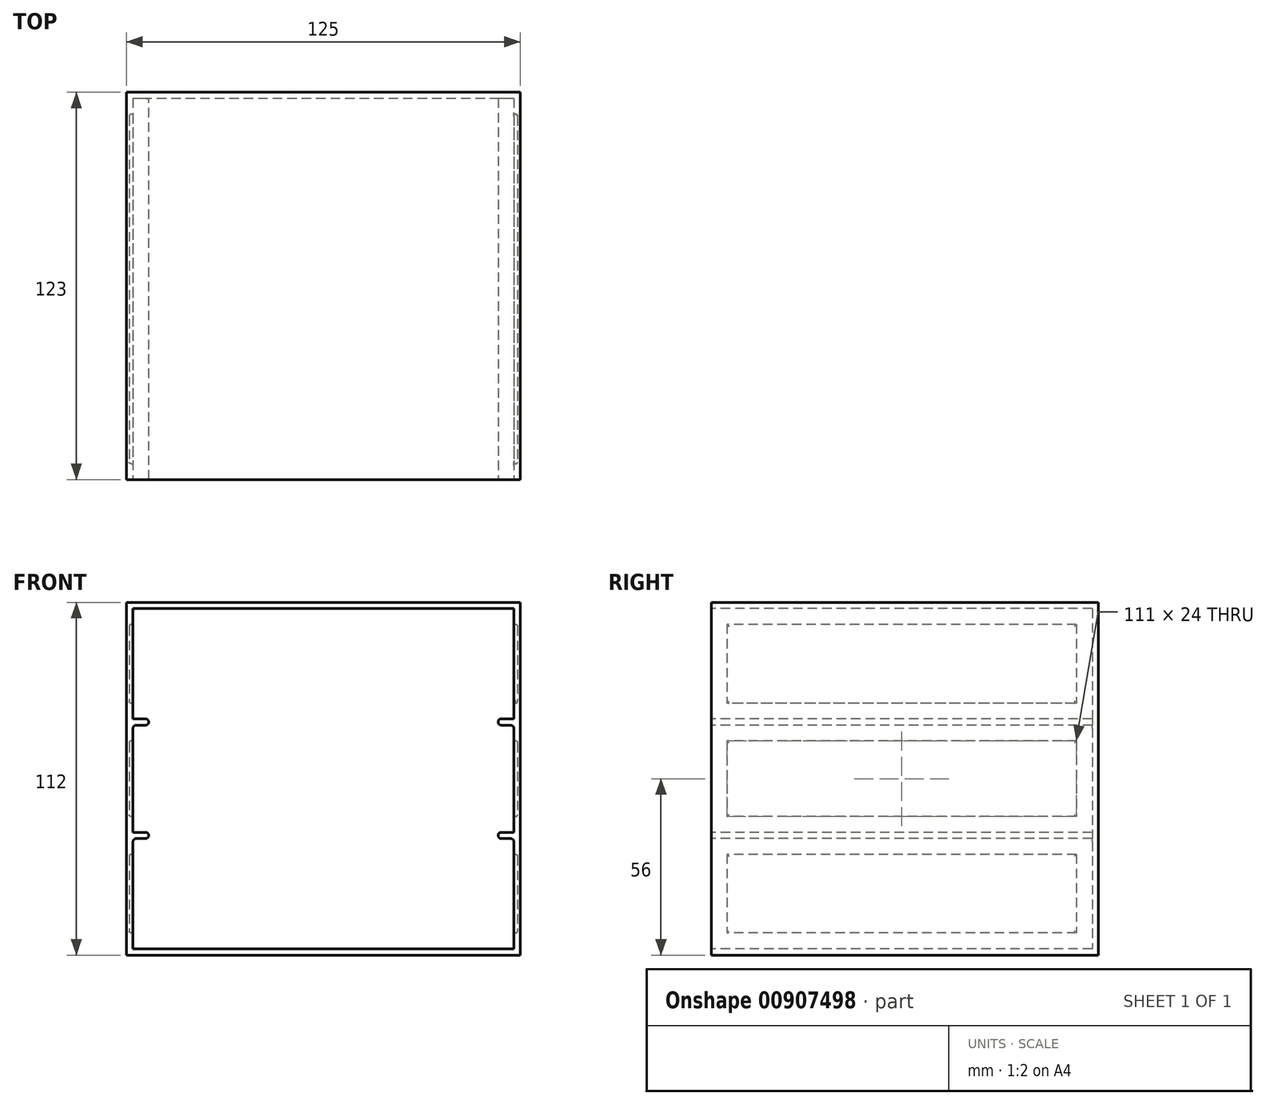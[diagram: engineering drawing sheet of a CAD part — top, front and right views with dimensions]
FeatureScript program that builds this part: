
annotation { "Feature Type Name" : "Feature", "Feature Type Description" : "" }
export const myFeature = defineFeature(function(context is Context, id is Id, definition is map)
    precondition{}
    {
        {
            var Q0;
            Q0=qCreatedBy(makeId("Top.planeOp"),FACE);
            var sketch = newSketch(context, id + "F0", { "sketchPlane" : qUnion([Q0])});
            skLineSegment(sketch, "E0.bottom", {"start": v(62.5, 61) * mm, "end": v(-62.5, 61) * mm});
            skLineSegment(sketch, "E0.top", {"start": v(62.5, -61) * mm, "end": v(-62.5, -61) * mm});
            skLineSegment(sketch, "E0.left", {"start": v(62.5, 61) * mm, "end": v(62.5, -61) * mm});
            skLineSegment(sketch, "E0.right", {"start": v(-62.5, 61) * mm, "end": v(-62.5, -61) * mm});
            skPoint(sketch, "E0.middle", {"position": v(0, 0) * mm});
            skSolve(sketch);
        }
        {
            var Q0;
            Q0=makeQuery(id+"F0.imprint","IMPRINT",FACE,{"disambiguationData":[TD([[makeQuery(id+"F0.imprint","IMPRINT",EDGE,{"derivedFrom":sQuery(id+"F0.wireOp",EDGE,"E0.bottom")}),1.0]])]});
            extrude(context, id + "F1", {"entities" : qUnion([Q0]), "depth" : 2 * mm, "offsetDistance" : 25 * mm});
        }
        {
            var Q0;
            Q0=makeQuery(id+"F1.opExtrude","CAP_FACE",FACE,{"disambiguationData":[OSD([sQuery(id+"F0.wireOp",EDGE,"E0.bottom"),sQuery(id+"F0.wireOp",EDGE,"E0.top"),sQuery(id+"F0.wireOp",EDGE,"E0.left"),sQuery(id+"F0.wireOp",EDGE,"E0.right")])],"isStart":false});
            var sketch = newSketch(context, id + "F2", { "sketchPlane" : qUnion([Q0])});
            skLineSegment(sketch, "E1.0", {"start": v(-60.5, 61) * mm, "end": v(-60.5, -61) * mm});
            skLineSegment(sketch, "E2.0", {"start": v(62.5, 59) * mm, "end": v(-62.5, 59) * mm});
            skLineSegment(sketch, "E3.0", {"start": v(60.5, 61) * mm, "end": v(60.5, -61) * mm});
            skSolve(sketch);
        }
        {
            var Q0;
            Q0=qSketchRegion(id+"F2",true);
            var Q1;
            {var subQ0=sQuery(id+"F2.wireOp",EDGE,"E1.0");var subQ1=makeQuery(id+"F1.opExtrude","CAP_EDGE",EDGE,{"disambiguationData":[OSD([sQuery(id+"F0.wireOp",EDGE,"E0.bottom")])],"isStart":false});var subQ2=makeQuery(id+"F2.imprint","INTERSECT",VERTEX,{"derivedFrom":[subQ1,subQ0]});Q1=makeQuery(id+"F2.imprint","IMPRINT",FACE,{"disambiguationData":[TD([[makeQuery(id+"F2.imprint","IMPRINT",EDGE,{"disambiguationData":[TD([[subQ2,-1.0]])],"derivedFrom":subQ0}),1.0]])]});}
            var Q2;
            {var subQ0=sQuery(id+"F2.wireOp",EDGE,"E1.0");var subQ1=makeQuery(id+"F1.opExtrude","CAP_EDGE",EDGE,{"disambiguationData":[OSD([sQuery(id+"F0.wireOp",EDGE,"E0.bottom")])],"isStart":false});var subQ2=makeQuery(id+"F2.imprint","INTERSECT",VERTEX,{"derivedFrom":[subQ1,subQ0]});Q2=makeQuery(id+"F2.imprint","IMPRINT",FACE,{"disambiguationData":[TD([[makeQuery(id+"F2.imprint","IMPRINT",EDGE,{"disambiguationData":[TD([[subQ2,-1.0]])],"derivedFrom":subQ0}),-1.0]])]});}
            var Q3;
            {var subQ0=sQuery(id+"F2.wireOp",EDGE,"E1.0");var subQ1=makeQuery(id+"F1.opExtrude","CAP_EDGE",EDGE,{"disambiguationData":[OSD([sQuery(id+"F0.wireOp",EDGE,"E0.top")])],"isStart":false});var subQ2=makeQuery(id+"F2.imprint","INTERSECT",VERTEX,{"derivedFrom":[subQ1,subQ0]});Q3=makeQuery(id+"F2.imprint","IMPRINT",FACE,{"disambiguationData":[TD([[makeQuery(id+"F2.imprint","IMPRINT",EDGE,{"disambiguationData":[TD([[subQ2,1.0]])],"derivedFrom":subQ0}),-1.0]])]});}
            var Q4;
            {var subQ0=sQuery(id+"F2.wireOp",EDGE,"E2.0");var subQ1=makeQuery(id+"F1.opExtrude","CAP_EDGE",EDGE,{"disambiguationData":[OSD([sQuery(id+"F0.wireOp",EDGE,"E0.left")])],"isStart":false});var subQ2=makeQuery(id+"F2.imprint","INTERSECT",VERTEX,{"derivedFrom":[subQ1,subQ0]});Q4=makeQuery(id+"F2.imprint","IMPRINT",FACE,{"disambiguationData":[TD([[makeQuery(id+"F2.imprint","IMPRINT",EDGE,{"disambiguationData":[TD([[subQ2,-1.0]])],"derivedFrom":subQ0}),1.0]])]});}
            var Q5;
            {var subQ0=sQuery(id+"F2.wireOp",EDGE,"E2.0");var subQ1=makeQuery(id+"F1.opExtrude","CAP_EDGE",EDGE,{"disambiguationData":[OSD([sQuery(id+"F0.wireOp",EDGE,"E0.left")])],"isStart":false});var subQ2=makeQuery(id+"F2.imprint","INTERSECT",VERTEX,{"derivedFrom":[subQ1,subQ0]});Q5=makeQuery(id+"F2.imprint","IMPRINT",FACE,{"disambiguationData":[TD([[makeQuery(id+"F2.imprint","IMPRINT",EDGE,{"disambiguationData":[TD([[subQ2,-1.0]])],"derivedFrom":subQ0}),-1.0]])]});}
            extrude(context, id + "F3", {"entities" : qUnion([Q0, Q1, Q2, Q3, Q4, Q5]), "operationType" : NewBodyOperationType.ADD, "depth" : 108 * mm, "offsetDistance" : 25 * mm});
        }
        {
            var Q0;
            Q0=makeQuery(id+"F3.opExtrude","CAP_FACE",FACE,{"disambiguationData":[OSD([sQuery(id+"F0.wireOp",EDGE,"E0.bottom"),sQuery(id+"F0.wireOp",EDGE,"E0.top"),sQuery(id+"F0.wireOp",EDGE,"E0.left"),sQuery(id+"F0.wireOp",EDGE,"E0.right"),sQuery(id+"F2.wireOp",EDGE,"E1.0"),sQuery(id+"F2.wireOp",EDGE,"E2.0"),sQuery(id+"F2.wireOp",EDGE,"E3.0")])],"isStart":false});
            var sketch = newSketch(context, id + "F4", { "sketchPlane" : qUnion([Q0])});
            skLineSegment(sketch, "E4.bottom", {"start": v(-62.5, 61) * mm, "end": v(62.5, 61) * mm});
            skLineSegment(sketch, "E4.top", {"start": v(-62.5, -61) * mm, "end": v(62.5, -61) * mm});
            skLineSegment(sketch, "E4.left", {"start": v(-62.5, 61) * mm, "end": v(-62.5, -61) * mm});
            skLineSegment(sketch, "E4.right", {"start": v(62.5, 61) * mm, "end": v(62.5, -61) * mm});
            skSolve(sketch);
        }
        {
            var Q0;
            Q0=qSketchRegion(id+"F4",true);
            extrude(context, id + "F5", {"entities" : qUnion([Q0]), "operationType" : NewBodyOperationType.ADD, "depth" : 2 * mm, "offsetDistance" : 25 * mm});
        }
        {
            var Q0;
            {var subQ0=sQuery(id+"F0.wireOp",EDGE,"E0.top");var subQ1=makeQuery(id+"F1.opExtrude","CAP_EDGE",EDGE,{"disambiguationData":[OSD([subQ0])],"isStart":false});Q0=makeQuery(id+"F5.boolean.opBoolean","MERGE",FACE,{"derivedFrom":[makeQuery(id+"F3.boolean.opBoolean","MERGE",FACE,{"derivedFrom":[makeQuery(id+"F1.opExtrude","SWEPT_FACE",FACE,{"disambiguationData":[OSD([subQ0])]}),makeQuery(id+"F3.opExtrude","SWEPT_FACE",FACE,{"disambiguationData":[OSD([subQ0]),TDD([makeQuery(id+"F2.imprint","IMPRINT",EDGE,{"disambiguationData":[TD([[makeQuery(id+"F2.imprint","INTERSECT",VERTEX,{"derivedFrom":[subQ1,makeQuery(id+"F1.opExtrude","CAP_EDGE",EDGE,{"disambiguationData":[OSD([sQuery(id+"F0.wireOp",EDGE,"E0.left")])],"isStart":false})]}),-1.0]])],"derivedFrom":subQ1})])]}),makeQuery(id+"F3.opExtrude","SWEPT_FACE",FACE,{"disambiguationData":[OSD([subQ0]),TDD([makeQuery(id+"F2.imprint","IMPRINT",EDGE,{"disambiguationData":[TD([[makeQuery(id+"F2.imprint","INTERSECT",VERTEX,{"derivedFrom":[subQ1,makeQuery(id+"F1.opExtrude","CAP_EDGE",EDGE,{"disambiguationData":[OSD([sQuery(id+"F0.wireOp",EDGE,"E0.right")])],"isStart":false})]}),1.0]])],"derivedFrom":subQ1})])]})]}),makeQuery(id+"F5.opExtrude","SWEPT_FACE",FACE,{"disambiguationData":[OSD([sQuery(id+"F4.wireOp",EDGE,"E4.top")])]})]});}
            var sketch = newSketch(context, id + "F6", { "sketchPlane" : qUnion([Q0])});
            skLineSegment(sketch, "E5.0", {"start": v(60.5, 38) * mm, "end": v(-60.5, 38) * mm});
            skLineSegment(sketch, "E6.0", {"start": v(60.5, 74) * mm, "end": v(-60.5, 74) * mm});
            skLineSegment(sketch, "E7.0", {"start": v(60.5, 39) * mm, "end": v(-60.5, 39) * mm});
            skLineSegment(sketch, "E8.0", {"start": v(60.5, 37) * mm, "end": v(-60.5, 37) * mm});
            skLineSegment(sketch, "E9.0", {"start": v(60.5, 75) * mm, "end": v(-60.5, 75) * mm});
            skLineSegment(sketch, "E10.0", {"start": v(60.5, 73) * mm, "end": v(-60.5, 73) * mm});
            skLineSegment(sketch, "E11.0", {"start": v(-55.5, 110) * mm, "end": v(-55.5, 2) * mm});
            skLineSegment(sketch, "E12.0", {"start": v(55.5, 110) * mm, "end": v(55.5, 2) * mm});
            skSolve(sketch);
        }
        {
            var Q0;
            {var subQ0=sQuery(id+"F6.wireOp",EDGE,"E6.0");var subQ3=sQuery(id+"F6.wireOp",EDGE,"E11.0");var subQ4=makeQuery(id+"F6.imprint","INTERSECT",VERTEX,{"derivedFrom":[subQ0,subQ3]});Q0=makeQuery(id+"F6.imprint","IMPRINT",FACE,{"disambiguationData":[TD([[makeQuery(id+"F6.imprint","IMPRINT",EDGE,{"disambiguationData":[TD([[subQ4,1.0]])],"derivedFrom":subQ3}),-1.0]])]});}
            var Q1;
            {var subQ0=sQuery(id+"F6.wireOp",EDGE,"E6.0");var subQ3=sQuery(id+"F6.wireOp",EDGE,"E11.0");var subQ4=makeQuery(id+"F6.imprint","INTERSECT",VERTEX,{"derivedFrom":[subQ0,subQ3]});Q1=makeQuery(id+"F6.imprint","IMPRINT",FACE,{"disambiguationData":[TD([[makeQuery(id+"F6.imprint","IMPRINT",EDGE,{"disambiguationData":[TD([[subQ4,-1.0]])],"derivedFrom":subQ3}),-1.0]])]});}
            var Q2;
            {var subQ0=sQuery(id+"F6.wireOp",EDGE,"E5.0");var subQ3=sQuery(id+"F6.wireOp",EDGE,"E11.0");var subQ4=makeQuery(id+"F6.imprint","INTERSECT",VERTEX,{"derivedFrom":[subQ0,subQ3]});Q2=makeQuery(id+"F6.imprint","IMPRINT",FACE,{"disambiguationData":[TD([[makeQuery(id+"F6.imprint","IMPRINT",EDGE,{"disambiguationData":[TD([[subQ4,1.0]])],"derivedFrom":subQ3}),-1.0]])]});}
            var Q3;
            {var subQ0=sQuery(id+"F6.wireOp",EDGE,"E5.0");var subQ3=sQuery(id+"F6.wireOp",EDGE,"E11.0");var subQ4=makeQuery(id+"F6.imprint","INTERSECT",VERTEX,{"derivedFrom":[subQ0,subQ3]});Q3=makeQuery(id+"F6.imprint","IMPRINT",FACE,{"disambiguationData":[TD([[makeQuery(id+"F6.imprint","IMPRINT",EDGE,{"disambiguationData":[TD([[subQ4,-1.0]])],"derivedFrom":subQ3}),-1.0]])]});}
            var Q4;
            {var subQ0=sQuery(id+"F6.wireOp",EDGE,"E6.0");var subQ3=sQuery(id+"F6.wireOp",EDGE,"E12.0");var subQ4=makeQuery(id+"F6.imprint","INTERSECT",VERTEX,{"derivedFrom":[subQ0,subQ3]});Q4=makeQuery(id+"F6.imprint","IMPRINT",FACE,{"disambiguationData":[TD([[makeQuery(id+"F6.imprint","IMPRINT",EDGE,{"disambiguationData":[TD([[subQ4,1.0]])],"derivedFrom":subQ3}),1.0]])]});}
            var Q5;
            {var subQ0=sQuery(id+"F6.wireOp",EDGE,"E6.0");var subQ3=sQuery(id+"F6.wireOp",EDGE,"E12.0");var subQ4=makeQuery(id+"F6.imprint","INTERSECT",VERTEX,{"derivedFrom":[subQ0,subQ3]});Q5=makeQuery(id+"F6.imprint","IMPRINT",FACE,{"disambiguationData":[TD([[makeQuery(id+"F6.imprint","IMPRINT",EDGE,{"disambiguationData":[TD([[subQ4,-1.0]])],"derivedFrom":subQ3}),1.0]])]});}
            var Q6;
            {var subQ0=sQuery(id+"F6.wireOp",EDGE,"E5.0");var subQ3=sQuery(id+"F6.wireOp",EDGE,"E12.0");var subQ4=makeQuery(id+"F6.imprint","INTERSECT",VERTEX,{"derivedFrom":[subQ0,subQ3]});Q6=makeQuery(id+"F6.imprint","IMPRINT",FACE,{"disambiguationData":[TD([[makeQuery(id+"F6.imprint","IMPRINT",EDGE,{"disambiguationData":[TD([[subQ4,1.0]])],"derivedFrom":subQ3}),1.0]])]});}
            var Q7;
            {var subQ0=sQuery(id+"F6.wireOp",EDGE,"E5.0");var subQ3=sQuery(id+"F6.wireOp",EDGE,"E12.0");var subQ4=makeQuery(id+"F6.imprint","INTERSECT",VERTEX,{"derivedFrom":[subQ0,subQ3]});Q7=makeQuery(id+"F6.imprint","IMPRINT",FACE,{"disambiguationData":[TD([[makeQuery(id+"F6.imprint","IMPRINT",EDGE,{"disambiguationData":[TD([[subQ4,-1.0]])],"derivedFrom":subQ3}),1.0]])]});}
            extrude(context, id + "F7", {"entities" : qUnion([Q0, Q1, Q2, Q3, Q4, Q5, Q6, Q7]), "operationType" : NewBodyOperationType.ADD, "oppositeDirection" : true, "depth" : 120 * mm, "offsetDistance" : 25 * mm});
        }
        {
            var Q0;
            {var subQ0=sQuery(id+"F6.wireOp",EDGE,"E11.0");var subQ1=sQuery(id+"F6.wireOp",EDGE,"E10.0");var subQ2=sQuery(id+"F6.wireOp",EDGE,"E9.0");var subQ3=sQuery(id+"F2.wireOp",EDGE,"E1.0");var subQ4=sQuery(id+"F0.wireOp",EDGE,"E0.top");var subQ5=sQuery(id+"F6.wireOp",EDGE,"E12.0");var subQ6=sQuery(id+"F2.wireOp",EDGE,"E3.0");var subQ7=sQuery(id+"F6.wireOp",EDGE,"E8.0");var subQ8=sQuery(id+"F6.wireOp",EDGE,"E7.0");var subQ9=makeQuery(id+"F1.opExtrude","CAP_EDGE",EDGE,{"disambiguationData":[OSD([subQ4])],"isStart":false});Q0=makeQuery(id+"F7.boolean.opBoolean","MERGE",FACE,{"derivedFrom":[makeQuery(id+"F5.boolean.opBoolean","MERGE",FACE,{"derivedFrom":[makeQuery(id+"F3.boolean.opBoolean","MERGE",FACE,{"derivedFrom":[makeQuery(id+"F1.opExtrude","SWEPT_FACE",FACE,{"disambiguationData":[OSD([subQ4])]}),makeQuery(id+"F3.opExtrude","SWEPT_FACE",FACE,{"disambiguationData":[OSD([subQ4]),TDD([makeQuery(id+"F2.imprint","IMPRINT",EDGE,{"disambiguationData":[TD([[makeQuery(id+"F2.imprint","INTERSECT",VERTEX,{"derivedFrom":[subQ9,makeQuery(id+"F1.opExtrude","CAP_EDGE",EDGE,{"disambiguationData":[OSD([sQuery(id+"F0.wireOp",EDGE,"E0.left")])],"isStart":false})]}),-1.0]])],"derivedFrom":subQ9})])]}),makeQuery(id+"F3.opExtrude","SWEPT_FACE",FACE,{"disambiguationData":[OSD([subQ4]),TDD([makeQuery(id+"F2.imprint","IMPRINT",EDGE,{"disambiguationData":[TD([[makeQuery(id+"F2.imprint","INTERSECT",VERTEX,{"derivedFrom":[subQ9,makeQuery(id+"F1.opExtrude","CAP_EDGE",EDGE,{"disambiguationData":[OSD([sQuery(id+"F0.wireOp",EDGE,"E0.right")])],"isStart":false})]}),1.0]])],"derivedFrom":subQ9})])]})]}),makeQuery(id+"F5.opExtrude","SWEPT_FACE",FACE,{"disambiguationData":[OSD([sQuery(id+"F4.wireOp",EDGE,"E4.top")])]})]}),makeQuery(id+"F7.opExtrude","CAP_FACE",FACE,{"disambiguationData":[OSD([subQ4,subQ6,subQ8,subQ7,subQ5])],"isStart":true}),makeQuery(id+"F7.opExtrude","CAP_FACE",FACE,{"disambiguationData":[OSD([subQ4,subQ3,subQ8,subQ7,subQ0])],"isStart":true}),makeQuery(id+"F7.opExtrude","CAP_FACE",FACE,{"disambiguationData":[OSD([subQ4,subQ6,subQ2,subQ1,subQ5])],"isStart":true}),makeQuery(id+"F7.opExtrude","CAP_FACE",FACE,{"disambiguationData":[OSD([subQ4,subQ3,subQ2,subQ1,subQ0])],"isStart":true})]});}
            extrude(context, id + "F8", {"entities" : qUnion([Q0]), "operationType" : NewBodyOperationType.ADD, "depth" : 1 * mm, "offsetDistance" : 25 * mm});
        }
        {
            var Q0;
            {var subQ0=sQuery(id+"F6.wireOp",EDGE,"E9.0");var subQ1=sQuery(id+"F2.wireOp",EDGE,"E1.0");var subQ2=sQuery(id+"F0.wireOp",EDGE,"E0.top");var subQ3=makeQuery(id+"F3.opExtrude","SWEPT_EDGE",EDGE,{"disambiguationData":[OSD([subQ2,subQ1])]});var subQ4=sQuery(id+"F6.wireOp",EDGE,"E11.0");var subQ5=makeQuery(id+"F7.opExtrude","SWEPT_FACE",FACE,{"disambiguationData":[OSD([subQ0]),TDD([makeQuery(id+"F6.imprint","IMPRINT",EDGE,{"disambiguationData":[TD([[makeQuery(id+"F6.imprint","INTERSECT",VERTEX,{"derivedFrom":[subQ0,subQ4]}),-1.0]])],"derivedFrom":subQ0})])]});var subQ20=makeQuery(id+"F3.opExtrude","SWEPT_FACE",FACE,{"disambiguationData":[OSD([subQ1])]});Q0=makeQuery(id+"F8.boolean.opBoolean","MERGE",FACE,{"derivedFrom":[makeQuery(id+"F7.boolean.opBoolean","SPLIT",FACE,{"disambiguationData":[TD([subQ5])],"derivedFrom":subQ20}),makeQuery(id+"F8.opExtrude","SWEPT_FACE",FACE,{"disambiguationData":[OSD([subQ2,subQ1]),TDD([makeQuery(id+"F7.boolean.opBoolean","SPLIT",EDGE,{"disambiguationData":[TD([subQ5])],"derivedFrom":subQ3})])]})]});}
            var sketch = newSketch(context, id + "F9", { "sketchPlane" : qUnion([Q0])});
            skLineSegment(sketch, "E13.0", {"start": v(54, 105) * mm, "end": v(-57, 105) * mm});
            skLineSegment(sketch, "E13.1", {"start": v(54, 105) * mm, "end": v(54, 80) * mm});
            skLineSegment(sketch, "E13.2", {"start": v(54, 80) * mm, "end": v(-57, 80) * mm});
            skLineSegment(sketch, "E13.3", {"start": v(-57, 105) * mm, "end": v(-57, 80) * mm});
            skLineSegment(sketch, "E14.0", {"start": v(54, 68) * mm, "end": v(-57, 68) * mm});
            skLineSegment(sketch, "E14.1", {"start": v(54, 68) * mm, "end": v(54, 44) * mm});
            skLineSegment(sketch, "E14.2", {"start": v(54, 44) * mm, "end": v(-57, 44) * mm});
            skLineSegment(sketch, "E14.3", {"start": v(-57, 68) * mm, "end": v(-57, 44) * mm});
            skLineSegment(sketch, "E15.0", {"start": v(54, 32) * mm, "end": v(-57, 32) * mm});
            skLineSegment(sketch, "E15.1", {"start": v(54, 32) * mm, "end": v(54, 7) * mm});
            skLineSegment(sketch, "E15.2", {"start": v(54, 7) * mm, "end": v(-57, 7) * mm});
            skLineSegment(sketch, "E15.3", {"start": v(-57, 32) * mm, "end": v(-57, 7) * mm});
            skSolve(sketch);
        }
        {
            var Q0;
            {var subQ4=sQuery(id+"F0.wireOp",EDGE,"E0.top");var subQ8=sQuery(id+"F6.wireOp",EDGE,"E12.0");var subQ9=sQuery(id+"F2.wireOp",EDGE,"E3.0");var subQ11=makeQuery(id+"F3.opExtrude","SWEPT_FACE",FACE,{"disambiguationData":[OSD([subQ9])]});var subQ13=sQuery(id+"F6.wireOp",EDGE,"E9.0");var subQ20=makeQuery(id+"F3.opExtrude","SWEPT_EDGE",EDGE,{"disambiguationData":[OSD([subQ4,subQ9])]});var subQ21=makeQuery(id+"F7.opExtrude","SWEPT_FACE",FACE,{"disambiguationData":[OSD([subQ13]),TDD([makeQuery(id+"F6.imprint","IMPRINT",EDGE,{"disambiguationData":[TD([[makeQuery(id+"F6.imprint","INTERSECT",VERTEX,{"derivedFrom":[subQ13,subQ8]}),1.0]])],"derivedFrom":subQ13})])]});Q0=makeQuery(id+"F8.boolean.opBoolean","MERGE",FACE,{"derivedFrom":[makeQuery(id+"F7.boolean.opBoolean","SPLIT",FACE,{"disambiguationData":[TD([subQ21])],"derivedFrom":subQ11}),makeQuery(id+"F8.opExtrude","SWEPT_FACE",FACE,{"disambiguationData":[OSD([subQ4,subQ9]),TDD([makeQuery(id+"F7.boolean.opBoolean","SPLIT",EDGE,{"disambiguationData":[TD([subQ21])],"derivedFrom":subQ20})])]})]});}
            var sketch = newSketch(context, id + "F10", { "sketchPlane" : qUnion([Q0])});
            skLineSegment(sketch, "E16.0", {"start": v(-54, 105) * mm, "end": v(57, 105) * mm});
            skLineSegment(sketch, "E16.1", {"start": v(-54, 105) * mm, "end": v(-54, 80) * mm});
            skLineSegment(sketch, "E16.2", {"start": v(-54, 80) * mm, "end": v(57, 80) * mm});
            skLineSegment(sketch, "E16.3", {"start": v(57, 105) * mm, "end": v(57, 80) * mm});
            skLineSegment(sketch, "E17.0", {"start": v(-54, 68) * mm, "end": v(57, 68) * mm});
            skLineSegment(sketch, "E17.1", {"start": v(-54, 68) * mm, "end": v(-54, 44) * mm});
            skLineSegment(sketch, "E17.2", {"start": v(-54, 44) * mm, "end": v(57, 44) * mm});
            skLineSegment(sketch, "E17.3", {"start": v(57, 68) * mm, "end": v(57, 44) * mm});
            skLineSegment(sketch, "E18.0", {"start": v(57, 32) * mm, "end": v(57, 7) * mm});
            skLineSegment(sketch, "E18.1", {"start": v(-54, 32) * mm, "end": v(57, 32) * mm});
            skLineSegment(sketch, "E18.2", {"start": v(-54, 32) * mm, "end": v(-54, 7) * mm});
            skLineSegment(sketch, "E18.3", {"start": v(-54, 7) * mm, "end": v(57, 7) * mm});
            skSolve(sketch);
        }
        {
            var Q0;
            Q0 = qSketchRegion(id + "F9", true);
            extrude(context, id + "F11", {"entities" : qUnion([Q0]), "operationType" : NewBodyOperationType.REMOVE, "oppositeDirection" : true, "depth" : 1.2 * mm, "offsetDistance" : 25 * mm});
        }
        {
            var Q0;
            Q0 = qSketchRegion(id + "F10", true);
            extrude(context, id + "F12", {"entities" : qUnion([Q0]), "operationType" : NewBodyOperationType.REMOVE, "oppositeDirection" : true, "depth" : 1.2 * mm, "offsetDistance" : 25 * mm});
        }
        {
            var Q0;
            Q0=makeQuery(id+"F7.opExtrude","SWEPT_EDGE",EDGE,{"disambiguationData":[OSD([sQuery(id+"F6.wireOp",EDGE,"E9.0"),sQuery(id+"F6.wireOp",EDGE,"E12.0")])]});
            var Q1;
            Q1=makeQuery(id+"F7.opExtrude","SWEPT_EDGE",EDGE,{"disambiguationData":[OSD([sQuery(id+"F6.wireOp",EDGE,"E10.0"),sQuery(id+"F6.wireOp",EDGE,"E12.0")])]});
            var Q2;
            Q2=makeQuery(id+"F7.opExtrude","SWEPT_EDGE",EDGE,{"disambiguationData":[OSD([sQuery(id+"F6.wireOp",EDGE,"E7.0"),sQuery(id+"F6.wireOp",EDGE,"E12.0")])]});
            var Q3;
            Q3=makeQuery(id+"F7.opExtrude","SWEPT_EDGE",EDGE,{"disambiguationData":[OSD([sQuery(id+"F6.wireOp",EDGE,"E8.0"),sQuery(id+"F6.wireOp",EDGE,"E12.0")])]});
            var Q4;
            Q4=makeQuery(id+"F7.opExtrude","SWEPT_EDGE",EDGE,{"disambiguationData":[OSD([sQuery(id+"F6.wireOp",EDGE,"E9.0"),sQuery(id+"F6.wireOp",EDGE,"E11.0")])]});
            var Q5;
            Q5=makeQuery(id+"F7.opExtrude","SWEPT_EDGE",EDGE,{"disambiguationData":[OSD([sQuery(id+"F6.wireOp",EDGE,"E10.0"),sQuery(id+"F6.wireOp",EDGE,"E11.0")])]});
            var Q6;
            Q6=makeQuery(id+"F7.opExtrude","SWEPT_EDGE",EDGE,{"disambiguationData":[OSD([sQuery(id+"F6.wireOp",EDGE,"E7.0"),sQuery(id+"F6.wireOp",EDGE,"E11.0")])]});
            var Q7;
            Q7=makeQuery(id+"F7.opExtrude","SWEPT_EDGE",EDGE,{"disambiguationData":[OSD([sQuery(id+"F6.wireOp",EDGE,"E8.0"),sQuery(id+"F6.wireOp",EDGE,"E11.0")])]});
            var Q8;
            Q8=makeQuery(id+"F7.opExtrude","SWEPT_EDGE",EDGE,{"disambiguationData":[OSD([sQuery(id+"F0.wireOp",EDGE,"E0.top"),sQuery(id+"F2.wireOp",EDGE,"E1.0"),sQuery(id+"F6.wireOp",EDGE,"E10.0")])]});
            var Q9;
            Q9=makeQuery(id+"F7.opExtrude","SWEPT_EDGE",EDGE,{"disambiguationData":[OSD([sQuery(id+"F0.wireOp",EDGE,"E0.top"),sQuery(id+"F2.wireOp",EDGE,"E1.0"),sQuery(id+"F6.wireOp",EDGE,"E8.0")])]});
            var Q10;
            Q10=makeQuery(id+"F7.opExtrude","SWEPT_EDGE",EDGE,{"disambiguationData":[OSD([sQuery(id+"F0.wireOp",EDGE,"E0.top"),sQuery(id+"F2.wireOp",EDGE,"E3.0"),sQuery(id+"F6.wireOp",EDGE,"E10.0")])]});
            var Q11;
            Q11=makeQuery(id+"F7.opExtrude","SWEPT_EDGE",EDGE,{"disambiguationData":[OSD([sQuery(id+"F0.wireOp",EDGE,"E0.top"),sQuery(id+"F2.wireOp",EDGE,"E3.0"),sQuery(id+"F6.wireOp",EDGE,"E8.0")])]});
            fillet(context, id + "F13", {"entities" : qUnion([Q0, Q1, Q2, Q3, Q4, Q5, Q6, Q7, Q8, Q9, Q10, Q11]), "radius" : 1 * mm, "tangentPropagation" : true, "allowEdgeOverflow" : false});
        }
        {
            var Q0;
            Q0=makeQuery(id+"F11.boolean.opBoolean","COPY",FACE,{"derivedFrom":makeQuery(id+"F11.opExtrude","CAP_FACE",FACE,{"disambiguationData":[OSD([sQuery(id+"F9.wireOp",EDGE,"aa4fbbbe-b9fa-4464-8a7d-c894082a82c9.0"),sQuery(id+"F9.wireOp",EDGE,"aa4fbbbe-b9fa-4464-8a7d-c894082a82c9.1"),sQuery(id+"F9.wireOp",EDGE,"aa4fbbbe-b9fa-4464-8a7d-c894082a82c9.2"),sQuery(id+"F9.wireOp",EDGE,"aa4fbbbe-b9fa-4464-8a7d-c894082a82c9.3")])],"isStart":false})});
            var Q1;
            Q1=makeQuery(id+"F11.boolean.opBoolean","COPY",EDGE,{"derivedFrom":makeQuery(id+"F11.opExtrude","CAP_EDGE",EDGE,{"disambiguationData":[OSD([sQuery(id+"F9.wireOp",EDGE,"aa4fbbbe-b9fa-4464-8a7d-c894082a82c9.3")])],"isStart":true})});
            var Q2;
            Q2=makeQuery(id+"F11.boolean.opBoolean","COPY",EDGE,{"derivedFrom":makeQuery(id+"F11.opExtrude","CAP_EDGE",EDGE,{"disambiguationData":[OSD([sQuery(id+"F9.wireOp",EDGE,"aa4fbbbe-b9fa-4464-8a7d-c894082a82c9.2")])],"isStart":true})});
            var Q3;
            Q3=makeQuery(id+"F11.boolean.opBoolean","COPY",EDGE,{"derivedFrom":makeQuery(id+"F11.opExtrude","CAP_EDGE",EDGE,{"disambiguationData":[OSD([sQuery(id+"F9.wireOp",EDGE,"aa4fbbbe-b9fa-4464-8a7d-c894082a82c9.0")])],"isStart":true})});
            var Q4;
            Q4=makeQuery(id+"F11.boolean.opBoolean","COPY",EDGE,{"derivedFrom":makeQuery(id+"F11.opExtrude","CAP_EDGE",EDGE,{"disambiguationData":[OSD([sQuery(id+"F9.wireOp",EDGE,"aa4fbbbe-b9fa-4464-8a7d-c894082a82c9.1")])],"isStart":true})});
            var Q5;
            Q5=makeQuery(id+"F11.boolean.opBoolean","COPY",FACE,{"derivedFrom":makeQuery(id+"F11.opExtrude","CAP_FACE",FACE,{"disambiguationData":[OSD([sQuery(id+"F9.wireOp",EDGE,"03dc7db1-e8f5-4956-9bfd-81e60578e748.0"),sQuery(id+"F9.wireOp",EDGE,"03dc7db1-e8f5-4956-9bfd-81e60578e748.1"),sQuery(id+"F9.wireOp",EDGE,"03dc7db1-e8f5-4956-9bfd-81e60578e748.2"),sQuery(id+"F9.wireOp",EDGE,"03dc7db1-e8f5-4956-9bfd-81e60578e748.3")])],"isStart":false})});
            var Q6;
            Q6=makeQuery(id+"F11.boolean.opBoolean","COPY",FACE,{"derivedFrom":makeQuery(id+"F11.opExtrude","CAP_FACE",FACE,{"disambiguationData":[OSD([sQuery(id+"F9.wireOp",EDGE,"E13.0"),sQuery(id+"F9.wireOp",EDGE,"E13.1"),sQuery(id+"F9.wireOp",EDGE,"E13.2"),sQuery(id+"F9.wireOp",EDGE,"E13.3")])],"isStart":false})});
            var Q7;
            Q7=makeQuery(id+"F11.boolean.opBoolean","COPY",EDGE,{"derivedFrom":makeQuery(id+"F11.opExtrude","CAP_EDGE",EDGE,{"disambiguationData":[OSD([sQuery(id+"F9.wireOp",EDGE,"03dc7db1-e8f5-4956-9bfd-81e60578e748.0")])],"isStart":true})});
            var Q8;
            Q8=makeQuery(id+"F11.boolean.opBoolean","COPY",EDGE,{"derivedFrom":makeQuery(id+"F11.opExtrude","CAP_EDGE",EDGE,{"disambiguationData":[OSD([sQuery(id+"F9.wireOp",EDGE,"03dc7db1-e8f5-4956-9bfd-81e60578e748.3")])],"isStart":true})});
            var Q9;
            Q9=makeQuery(id+"F11.boolean.opBoolean","COPY",EDGE,{"derivedFrom":makeQuery(id+"F11.opExtrude","CAP_EDGE",EDGE,{"disambiguationData":[OSD([sQuery(id+"F9.wireOp",EDGE,"03dc7db1-e8f5-4956-9bfd-81e60578e748.1")])],"isStart":true})});
            var Q10;
            Q10=makeQuery(id+"F11.boolean.opBoolean","COPY",EDGE,{"derivedFrom":makeQuery(id+"F11.opExtrude","CAP_EDGE",EDGE,{"disambiguationData":[OSD([sQuery(id+"F9.wireOp",EDGE,"03dc7db1-e8f5-4956-9bfd-81e60578e748.2")])],"isStart":true})});
            var Q11;
            Q11=makeQuery(id+"F11.boolean.opBoolean","COPY",EDGE,{"derivedFrom":makeQuery(id+"F11.opExtrude","CAP_EDGE",EDGE,{"disambiguationData":[OSD([sQuery(id+"F9.wireOp",EDGE,"E13.2")])],"isStart":true})});
            var Q12;
            Q12=makeQuery(id+"F11.boolean.opBoolean","COPY",EDGE,{"derivedFrom":makeQuery(id+"F11.opExtrude","CAP_EDGE",EDGE,{"disambiguationData":[OSD([sQuery(id+"F9.wireOp",EDGE,"E13.3")])],"isStart":true})});
            var Q13;
            Q13=makeQuery(id+"F11.boolean.opBoolean","COPY",EDGE,{"derivedFrom":makeQuery(id+"F11.opExtrude","CAP_EDGE",EDGE,{"disambiguationData":[OSD([sQuery(id+"F9.wireOp",EDGE,"E13.0")])],"isStart":true})});
            var Q14;
            Q14=makeQuery(id+"F11.boolean.opBoolean","COPY",EDGE,{"derivedFrom":makeQuery(id+"F11.opExtrude","CAP_EDGE",EDGE,{"disambiguationData":[OSD([sQuery(id+"F9.wireOp",EDGE,"E13.1")])],"isStart":true})});
            var Q15;
            Q15=makeQuery(id+"F11.boolean.opBoolean","COPY",FACE,{"derivedFrom":makeQuery(id+"F11.opExtrude","CAP_FACE",FACE,{"disambiguationData":[OSD([sQuery(id+"F9.wireOp",EDGE,"E14.0"),sQuery(id+"F9.wireOp",EDGE,"E14.1"),sQuery(id+"F9.wireOp",EDGE,"E14.2"),sQuery(id+"F9.wireOp",EDGE,"E14.3")])],"isStart":false})});
            var Q16;
            Q16=makeQuery(id+"F11.boolean.opBoolean","COPY",EDGE,{"derivedFrom":makeQuery(id+"F11.opExtrude","CAP_EDGE",EDGE,{"disambiguationData":[OSD([sQuery(id+"F9.wireOp",EDGE,"E14.0")])],"isStart":true})});
            var Q17;
            Q17=makeQuery(id+"F11.boolean.opBoolean","COPY",EDGE,{"derivedFrom":makeQuery(id+"F11.opExtrude","CAP_EDGE",EDGE,{"disambiguationData":[OSD([sQuery(id+"F9.wireOp",EDGE,"E14.3")])],"isStart":true})});
            var Q18;
            Q18=makeQuery(id+"F11.boolean.opBoolean","COPY",EDGE,{"derivedFrom":makeQuery(id+"F11.opExtrude","CAP_EDGE",EDGE,{"disambiguationData":[OSD([sQuery(id+"F9.wireOp",EDGE,"E14.1")])],"isStart":true})});
            var Q19;
            Q19=makeQuery(id+"F11.boolean.opBoolean","COPY",EDGE,{"derivedFrom":makeQuery(id+"F11.opExtrude","CAP_EDGE",EDGE,{"disambiguationData":[OSD([sQuery(id+"F9.wireOp",EDGE,"E14.2")])],"isStart":true})});
            var Q20;
            Q20=makeQuery(id+"F11.boolean.opBoolean","COPY",FACE,{"derivedFrom":makeQuery(id+"F11.opExtrude","CAP_FACE",FACE,{"disambiguationData":[OSD([sQuery(id+"F9.wireOp",EDGE,"E15.0"),sQuery(id+"F9.wireOp",EDGE,"E15.1"),sQuery(id+"F9.wireOp",EDGE,"E15.2"),sQuery(id+"F9.wireOp",EDGE,"E15.3")])],"isStart":false})});
            var Q21;
            Q21=makeQuery(id+"F11.boolean.opBoolean","COPY",EDGE,{"derivedFrom":makeQuery(id+"F11.opExtrude","CAP_EDGE",EDGE,{"disambiguationData":[OSD([sQuery(id+"F9.wireOp",EDGE,"E15.0")])],"isStart":true})});
            var Q22;
            Q22=makeQuery(id+"F11.boolean.opBoolean","COPY",EDGE,{"derivedFrom":makeQuery(id+"F11.opExtrude","CAP_EDGE",EDGE,{"disambiguationData":[OSD([sQuery(id+"F9.wireOp",EDGE,"E15.3")])],"isStart":true})});
            var Q23;
            Q23=makeQuery(id+"F11.boolean.opBoolean","COPY",EDGE,{"derivedFrom":makeQuery(id+"F11.opExtrude","CAP_EDGE",EDGE,{"disambiguationData":[OSD([sQuery(id+"F9.wireOp",EDGE,"E15.2")])],"isStart":true})});
            var Q24;
            Q24=makeQuery(id+"F12.boolean.opBoolean","COPY",FACE,{"derivedFrom":makeQuery(id+"F12.opExtrude","CAP_FACE",FACE,{"disambiguationData":[OSD([sQuery(id+"F10.wireOp",EDGE,"E18.0"),sQuery(id+"F10.wireOp",EDGE,"E18.1"),sQuery(id+"F10.wireOp",EDGE,"E18.2"),sQuery(id+"F10.wireOp",EDGE,"E18.3")])],"isStart":false})});
            var Q25;
            Q25=makeQuery(id+"F12.boolean.opBoolean","COPY",FACE,{"derivedFrom":makeQuery(id+"F12.opExtrude","CAP_FACE",FACE,{"disambiguationData":[OSD([sQuery(id+"F10.wireOp",EDGE,"E17.0"),sQuery(id+"F10.wireOp",EDGE,"E17.1"),sQuery(id+"F10.wireOp",EDGE,"E17.2"),sQuery(id+"F10.wireOp",EDGE,"E17.3")])],"isStart":false})});
            var Q26;
            Q26=makeQuery(id+"F12.boolean.opBoolean","COPY",FACE,{"derivedFrom":makeQuery(id+"F12.opExtrude","CAP_FACE",FACE,{"disambiguationData":[OSD([sQuery(id+"F10.wireOp",EDGE,"E16.0"),sQuery(id+"F10.wireOp",EDGE,"E16.1"),sQuery(id+"F10.wireOp",EDGE,"E16.2"),sQuery(id+"F10.wireOp",EDGE,"E16.3")])],"isStart":false})});
            var Q27;
            Q27=makeQuery(id+"F12.boolean.opBoolean","COPY",EDGE,{"derivedFrom":makeQuery(id+"F12.opExtrude","CAP_EDGE",EDGE,{"disambiguationData":[OSD([sQuery(id+"F10.wireOp",EDGE,"E16.0")])],"isStart":true})});
            var Q28;
            Q28=makeQuery(id+"F12.boolean.opBoolean","COPY",EDGE,{"derivedFrom":makeQuery(id+"F12.opExtrude","CAP_EDGE",EDGE,{"disambiguationData":[OSD([sQuery(id+"F10.wireOp",EDGE,"E16.1")])],"isStart":true})});
            var Q29;
            Q29=makeQuery(id+"F12.boolean.opBoolean","COPY",EDGE,{"derivedFrom":makeQuery(id+"F12.opExtrude","CAP_EDGE",EDGE,{"disambiguationData":[OSD([sQuery(id+"F10.wireOp",EDGE,"E16.3")])],"isStart":true})});
            var Q30;
            Q30=makeQuery(id+"F12.boolean.opBoolean","COPY",FACE,{"derivedFrom":makeQuery(id+"F12.opExtrude","SWEPT_FACE",FACE,{"disambiguationData":[OSD([sQuery(id+"F10.wireOp",EDGE,"E16.2")])]})});
            var Q31;
            Q31=makeQuery(id+"F12.boolean.opBoolean","COPY",EDGE,{"derivedFrom":makeQuery(id+"F12.opExtrude","CAP_EDGE",EDGE,{"disambiguationData":[OSD([sQuery(id+"F10.wireOp",EDGE,"E17.0")])],"isStart":true})});
            var Q32;
            Q32=makeQuery(id+"F12.boolean.opBoolean","COPY",EDGE,{"derivedFrom":makeQuery(id+"F12.opExtrude","CAP_EDGE",EDGE,{"disambiguationData":[OSD([sQuery(id+"F10.wireOp",EDGE,"E17.3")])],"isStart":true})});
            var Q33;
            Q33=makeQuery(id+"F12.boolean.opBoolean","COPY",EDGE,{"derivedFrom":makeQuery(id+"F12.opExtrude","CAP_EDGE",EDGE,{"disambiguationData":[OSD([sQuery(id+"F10.wireOp",EDGE,"E17.1")])],"isStart":true})});
            var Q34;
            Q34=makeQuery(id+"F12.boolean.opBoolean","COPY",EDGE,{"derivedFrom":makeQuery(id+"F12.opExtrude","CAP_EDGE",EDGE,{"disambiguationData":[OSD([sQuery(id+"F10.wireOp",EDGE,"E17.2")])],"isStart":true})});
            var Q35;
            Q35=makeQuery(id+"F12.boolean.opBoolean","COPY",EDGE,{"derivedFrom":makeQuery(id+"F12.opExtrude","CAP_EDGE",EDGE,{"disambiguationData":[OSD([sQuery(id+"F10.wireOp",EDGE,"E18.2")])],"isStart":true})});
            var Q36;
            Q36=makeQuery(id+"F12.boolean.opBoolean","COPY",EDGE,{"derivedFrom":makeQuery(id+"F12.opExtrude","CAP_EDGE",EDGE,{"disambiguationData":[OSD([sQuery(id+"F10.wireOp",EDGE,"E18.1")])],"isStart":true})});
            var Q37;
            Q37=makeQuery(id+"F12.boolean.opBoolean","COPY",EDGE,{"derivedFrom":makeQuery(id+"F12.opExtrude","CAP_EDGE",EDGE,{"disambiguationData":[OSD([sQuery(id+"F10.wireOp",EDGE,"E18.3")])],"isStart":true})});
            var Q38;
            Q38=makeQuery(id+"F12.boolean.opBoolean","COPY",EDGE,{"derivedFrom":makeQuery(id+"F12.opExtrude","CAP_EDGE",EDGE,{"disambiguationData":[OSD([sQuery(id+"F10.wireOp",EDGE,"E18.0")])],"isStart":true})});
            fillet(context, id + "F14", {"entities" : qUnion([Q0, Q1, Q2, Q3, Q4, Q5, Q6, Q7, Q8, Q9, Q10, Q11, Q12, Q13, Q14, Q15, Q16, Q17, Q18, Q19, Q20, Q21, Q22, Q23, Q24, Q25, Q26, Q27, Q28, Q29, Q30, Q31, Q32, Q33, Q34, Q35, Q36, Q37, Q38]), "radius" : .6 * mm, "tangentPropagation" : true, "allowEdgeOverflow" : false});
        }
    });
